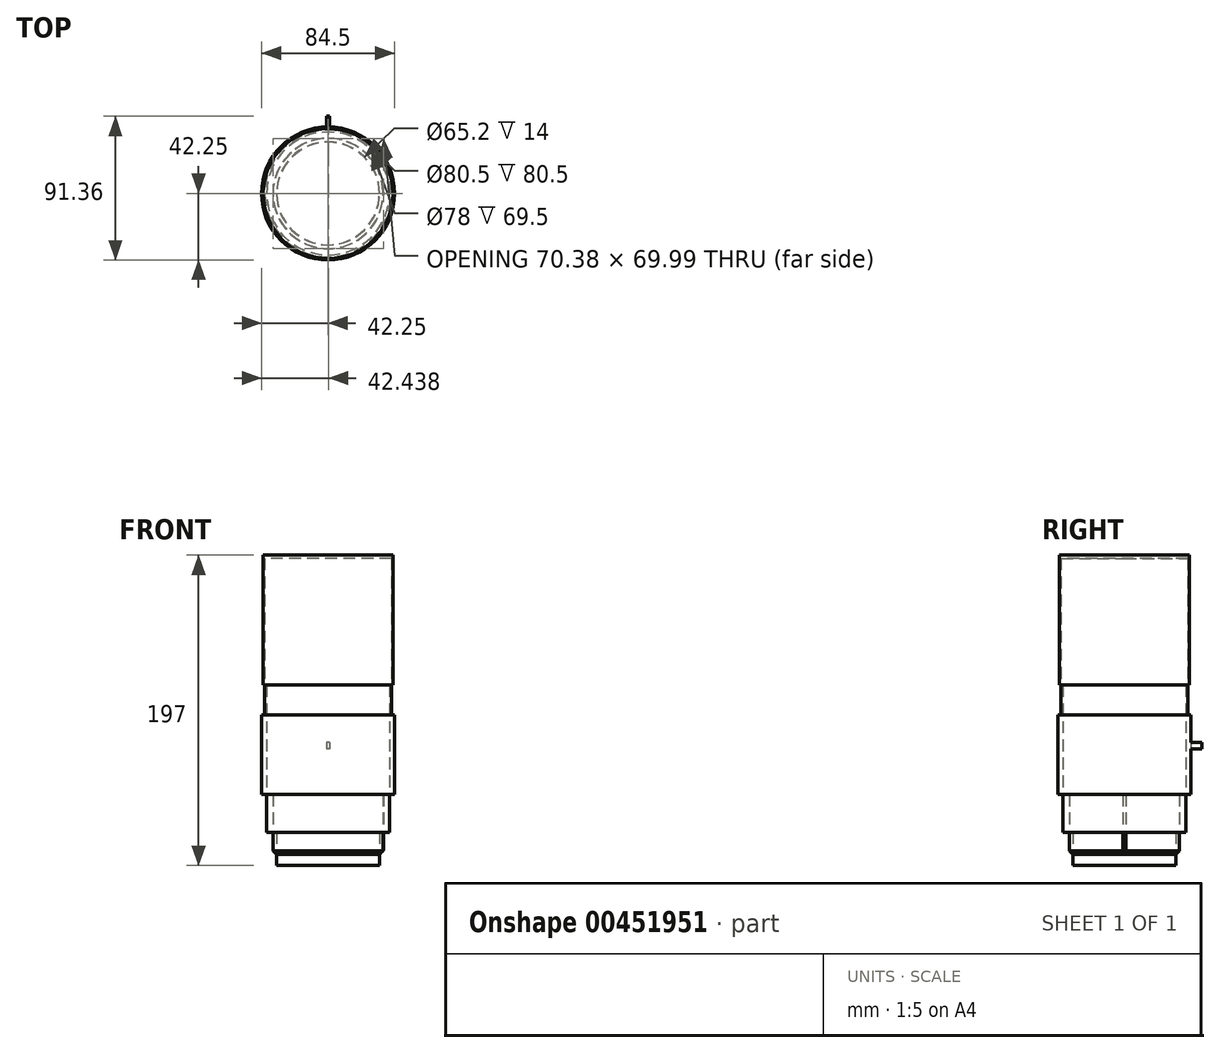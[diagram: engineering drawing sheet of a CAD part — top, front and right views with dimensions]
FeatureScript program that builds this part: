
annotation { "Feature Type Name" : "Feature", "Feature Type Description" : "" }
export const myFeature = defineFeature(function(context is Context, id is Id, definition is map)
    precondition{}
    {
        {
            var Q0;
            Q0=qCreatedBy(makeId("Top.planeOp"),FACE);
            var sketch = newSketch(context, id + "F0", { "sketchPlane" : qUnion([Q0])});
            skCircle(sketch, "E0", {"center": v(0, 0) * mm, "radius": 32.6 * mm});
            skSolve(sketch);
        }
        {
            var Q0;
            Q0=makeQuery(id+"F0.imprint","IMPRINT",FACE,{"disambiguationData":[TD([[makeQuery(id+"F0.imprint","IMPRINT",EDGE,{"derivedFrom":sQuery(id+"F0.wireOp",EDGE,"E0")}),1.0]])]});
            extrude(context, id + "F1", {"entities" : qUnion([Q0]), "depth" : 7 * mm});
        }
        {
            var Q0;
            Q0=makeQuery(id+"F1.opExtrude","CAP_FACE",FACE,{"disambiguationData":[OSD([sQuery(id+"F0.wireOp",EDGE,"E0")])],"isStart":false});
            var sketch = newSketch(context, id + "F2", { "sketchPlane" : qUnion([Q0])});
            skCircle(sketch, "E1", {"center": v(0, 0) * mm, "radius": 35 * mm});
            skSolve(sketch);
        }
        {
            var Q0;
            Q0=makeQuery(id+"F2.imprint","IMPRINT",FACE,{"disambiguationData":[TD([[makeQuery(id+"F2.imprint","IMPRINT",EDGE,{"derivedFrom":sQuery(id+"F2.wireOp",EDGE,"E1")}),1.0]])]});
            extrude(context, id + "F3", {"entities" : qUnion([Q0]), "depth" : 14 * mm});
        }
        {
            var Q0;
            Q0=makeQuery(id+"F3.opExtrude","CAP_EDGE",EDGE,{"disambiguationData":[OSD([sQuery(id+"F2.wireOp",EDGE,"E1")])],"isStart":true});
            chamfer(context, id + "F4", {"entities" : qUnion([Q0]), "chamferType" : ChamferType.OFFSET_ANGLE, "width" : 2.3 * mm, "oppositeDirection" : false, "angle" : 45 * degree, "tangentPropagation" : true});
        }
        {
            var Q0;
            Q0=makeQuery(id+"F3.opExtrude","CAP_FACE",FACE,{"disambiguationData":[OSD([sQuery(id+"F0.wireOp",EDGE,"E0"),sQuery(id+"F2.wireOp",EDGE,"E1")])],"isStart":false});
            var sketch = newSketch(context, id + "F5", { "sketchPlane" : qUnion([Q0])});
            skLineSegment(sketch, "E2.bottom", {"start": v(35.38, 0.9) * mm, "end": v(34.08, 0.9) * mm});
            skLineSegment(sketch, "E2.top", {"start": v(35.38, -0.9) * mm, "end": v(34.08, -0.9) * mm});
            skLineSegment(sketch, "E2.left", {"start": v(35.38, 0.9) * mm, "end": v(35.38, -0.9) * mm});
            skLineSegment(sketch, "E2.right", {"start": v(34.08, 0.9) * mm, "end": v(34.08, -0.9) * mm});
            skSolve(sketch);
        }
        {
            var Q0;
            Q0=qCreatedBy(makeId("Front.planeOp"),FACE);
            var sketch = newSketch(context, id + "F6", { "sketchPlane" : qUnion([Q0])});
            skLineSegment(sketch, "E3", {"start": v(0, 0) * mm, "end": v(0, 41.82) * mm});
            skSolve(sketch);
        }
        {
            var Q0;
            Q0=makeQuery(id+"FMMGtIccV8ZqxvP_2.16.F5.imprint","IMPRINT",FACE,{"disambiguationData":[TD([[makeQuery(id+"FMMGtIccV8ZqxvP_2.16.F5.imprint","IMPRINT",EDGE,{"derivedFrom":sQuery(id+"FMMGtIccV8ZqxvP_2.16.F5.wireOp",EDGE,"E2.bottom")}),1.0]])]});
            var Q1;
            Q1=makeQuery(id+"FMMGtIccV8ZqxvP_2.15.F5.imprint","IMPRINT",FACE,{"disambiguationData":[TD([[makeQuery(id+"FMMGtIccV8ZqxvP_2.15.F5.imprint","IMPRINT",EDGE,{"derivedFrom":sQuery(id+"FMMGtIccV8ZqxvP_2.15.F5.wireOp",EDGE,"E2.bottom")}),1.0]])]});
            var Q2;
            Q2=makeQuery(id+"FMMGtIccV8ZqxvP_2.14.F5.imprint","IMPRINT",FACE,{"disambiguationData":[TD([[makeQuery(id+"FMMGtIccV8ZqxvP_2.14.F5.imprint","IMPRINT",EDGE,{"derivedFrom":sQuery(id+"FMMGtIccV8ZqxvP_2.14.F5.wireOp",EDGE,"E2.bottom")}),1.0]])]});
            var Q3;
            Q3=makeQuery(id+"FMMGtIccV8ZqxvP_2.13.F5.imprint","IMPRINT",FACE,{"disambiguationData":[TD([[makeQuery(id+"FMMGtIccV8ZqxvP_2.13.F5.imprint","IMPRINT",EDGE,{"derivedFrom":sQuery(id+"FMMGtIccV8ZqxvP_2.13.F5.wireOp",EDGE,"E2.bottom")}),1.0]])]});
            var Q4;
            Q4=makeQuery(id+"FMMGtIccV8ZqxvP_2.12.F5.imprint","IMPRINT",FACE,{"disambiguationData":[TD([[makeQuery(id+"FMMGtIccV8ZqxvP_2.12.F5.imprint","IMPRINT",EDGE,{"derivedFrom":sQuery(id+"FMMGtIccV8ZqxvP_2.12.F5.wireOp",EDGE,"E2.bottom")}),1.0]])]});
            var Q5;
            Q5=makeQuery(id+"FMMGtIccV8ZqxvP_2.11.F5.imprint","IMPRINT",FACE,{"disambiguationData":[TD([[makeQuery(id+"FMMGtIccV8ZqxvP_2.11.F5.imprint","IMPRINT",EDGE,{"derivedFrom":sQuery(id+"FMMGtIccV8ZqxvP_2.11.F5.wireOp",EDGE,"E2.bottom")}),1.0]])]});
            var Q6;
            Q6=makeQuery(id+"FMMGtIccV8ZqxvP_2.10.F5.imprint","IMPRINT",FACE,{"disambiguationData":[TD([[makeQuery(id+"FMMGtIccV8ZqxvP_2.10.F5.imprint","IMPRINT",EDGE,{"derivedFrom":sQuery(id+"FMMGtIccV8ZqxvP_2.10.F5.wireOp",EDGE,"E2.bottom")}),1.0]])]});
            var Q7;
            Q7=makeQuery(id+"FMMGtIccV8ZqxvP_2.9.F5.imprint","IMPRINT",FACE,{"disambiguationData":[TD([[makeQuery(id+"FMMGtIccV8ZqxvP_2.9.F5.imprint","IMPRINT",EDGE,{"derivedFrom":sQuery(id+"FMMGtIccV8ZqxvP_2.9.F5.wireOp",EDGE,"E2.bottom")}),1.0]])]});
            var Q8;
            Q8=makeQuery(id+"FMMGtIccV8ZqxvP_2.8.F5.imprint","IMPRINT",FACE,{"disambiguationData":[TD([[makeQuery(id+"FMMGtIccV8ZqxvP_2.8.F5.imprint","IMPRINT",EDGE,{"derivedFrom":sQuery(id+"FMMGtIccV8ZqxvP_2.8.F5.wireOp",EDGE,"E2.bottom")}),1.0]])]});
            var Q9;
            Q9=makeQuery(id+"FMMGtIccV8ZqxvP_2.7.F5.imprint","IMPRINT",FACE,{"disambiguationData":[TD([[makeQuery(id+"FMMGtIccV8ZqxvP_2.7.F5.imprint","IMPRINT",EDGE,{"derivedFrom":sQuery(id+"FMMGtIccV8ZqxvP_2.7.F5.wireOp",EDGE,"E2.bottom")}),1.0]])]});
            var Q10;
            Q10=makeQuery(id+"FMMGtIccV8ZqxvP_2.6.F5.imprint","IMPRINT",FACE,{"disambiguationData":[TD([[makeQuery(id+"FMMGtIccV8ZqxvP_2.6.F5.imprint","IMPRINT",EDGE,{"derivedFrom":sQuery(id+"FMMGtIccV8ZqxvP_2.6.F5.wireOp",EDGE,"E2.bottom")}),1.0]])]});
            var Q11;
            Q11=makeQuery(id+"FMMGtIccV8ZqxvP_2.5.F5.imprint","IMPRINT",FACE,{"disambiguationData":[TD([[makeQuery(id+"FMMGtIccV8ZqxvP_2.5.F5.imprint","IMPRINT",EDGE,{"derivedFrom":sQuery(id+"FMMGtIccV8ZqxvP_2.5.F5.wireOp",EDGE,"E2.bottom")}),1.0]])]});
            var Q12;
            Q12=makeQuery(id+"FMMGtIccV8ZqxvP_2.4.F5.imprint","IMPRINT",FACE,{"disambiguationData":[TD([[makeQuery(id+"FMMGtIccV8ZqxvP_2.4.F5.imprint","IMPRINT",EDGE,{"derivedFrom":sQuery(id+"FMMGtIccV8ZqxvP_2.4.F5.wireOp",EDGE,"E2.bottom")}),1.0]])]});
            var Q13;
            Q13=makeQuery(id+"FMMGtIccV8ZqxvP_2.3.F5.imprint","IMPRINT",FACE,{"disambiguationData":[TD([[makeQuery(id+"FMMGtIccV8ZqxvP_2.3.F5.imprint","IMPRINT",EDGE,{"derivedFrom":sQuery(id+"FMMGtIccV8ZqxvP_2.3.F5.wireOp",EDGE,"E2.bottom")}),1.0]])]});
            var Q14;
            Q14=makeQuery(id+"FMMGtIccV8ZqxvP_2.2.F5.imprint","IMPRINT",FACE,{"disambiguationData":[TD([[makeQuery(id+"FMMGtIccV8ZqxvP_2.2.F5.imprint","IMPRINT",EDGE,{"derivedFrom":sQuery(id+"FMMGtIccV8ZqxvP_2.2.F5.wireOp",EDGE,"E2.bottom")}),1.0]])]});
            var Q15;
            Q15=makeQuery(id+"FMMGtIccV8ZqxvP_2.1.F5.imprint","IMPRINT",FACE,{"disambiguationData":[TD([[makeQuery(id+"FMMGtIccV8ZqxvP_2.1.F5.imprint","IMPRINT",EDGE,{"derivedFrom":sQuery(id+"FMMGtIccV8ZqxvP_2.1.F5.wireOp",EDGE,"E2.bottom")}),1.0]])]});
            var Q16;
            Q16=makeQuery(id+"FMMGtIccV8ZqxvP_2.49.F5.imprint","IMPRINT",FACE,{"disambiguationData":[TD([[makeQuery(id+"FMMGtIccV8ZqxvP_2.49.F5.imprint","IMPRINT",EDGE,{"derivedFrom":sQuery(id+"FMMGtIccV8ZqxvP_2.49.F5.wireOp",EDGE,"E2.bottom")}),1.0]])]});
            var Q17;
            Q17=makeQuery(id+"FMMGtIccV8ZqxvP_2.48.F5.imprint","IMPRINT",FACE,{"disambiguationData":[TD([[makeQuery(id+"FMMGtIccV8ZqxvP_2.48.F5.imprint","IMPRINT",EDGE,{"derivedFrom":sQuery(id+"FMMGtIccV8ZqxvP_2.48.F5.wireOp",EDGE,"E2.bottom")}),1.0]])]});
            var Q18;
            Q18=makeQuery(id+"FMMGtIccV8ZqxvP_2.47.F5.imprint","IMPRINT",FACE,{"disambiguationData":[TD([[makeQuery(id+"FMMGtIccV8ZqxvP_2.47.F5.imprint","IMPRINT",EDGE,{"derivedFrom":sQuery(id+"FMMGtIccV8ZqxvP_2.47.F5.wireOp",EDGE,"E2.bottom")}),1.0]])]});
            var Q19;
            Q19=makeQuery(id+"FMMGtIccV8ZqxvP_2.46.F5.imprint","IMPRINT",FACE,{"disambiguationData":[TD([[makeQuery(id+"FMMGtIccV8ZqxvP_2.46.F5.imprint","IMPRINT",EDGE,{"derivedFrom":sQuery(id+"FMMGtIccV8ZqxvP_2.46.F5.wireOp",EDGE,"E2.bottom")}),1.0]])]});
            var Q20;
            Q20=makeQuery(id+"FMMGtIccV8ZqxvP_2.45.F5.imprint","IMPRINT",FACE,{"disambiguationData":[TD([[makeQuery(id+"FMMGtIccV8ZqxvP_2.45.F5.imprint","IMPRINT",EDGE,{"derivedFrom":sQuery(id+"FMMGtIccV8ZqxvP_2.45.F5.wireOp",EDGE,"E2.bottom")}),1.0]])]});
            var Q21;
            Q21=makeQuery(id+"FMMGtIccV8ZqxvP_2.44.F5.imprint","IMPRINT",FACE,{"disambiguationData":[TD([[makeQuery(id+"FMMGtIccV8ZqxvP_2.44.F5.imprint","IMPRINT",EDGE,{"derivedFrom":sQuery(id+"FMMGtIccV8ZqxvP_2.44.F5.wireOp",EDGE,"E2.bottom")}),1.0]])]});
            var Q22;
            Q22=makeQuery(id+"FMMGtIccV8ZqxvP_2.43.F5.imprint","IMPRINT",FACE,{"disambiguationData":[TD([[makeQuery(id+"FMMGtIccV8ZqxvP_2.43.F5.imprint","IMPRINT",EDGE,{"derivedFrom":sQuery(id+"FMMGtIccV8ZqxvP_2.43.F5.wireOp",EDGE,"E2.bottom")}),1.0]])]});
            var Q23;
            Q23=makeQuery(id+"FMMGtIccV8ZqxvP_2.42.F5.imprint","IMPRINT",FACE,{"disambiguationData":[TD([[makeQuery(id+"FMMGtIccV8ZqxvP_2.42.F5.imprint","IMPRINT",EDGE,{"derivedFrom":sQuery(id+"FMMGtIccV8ZqxvP_2.42.F5.wireOp",EDGE,"E2.bottom")}),1.0]])]});
            var Q24;
            Q24=makeQuery(id+"FMMGtIccV8ZqxvP_2.40.F5.imprint","IMPRINT",FACE,{"disambiguationData":[TD([[makeQuery(id+"FMMGtIccV8ZqxvP_2.40.F5.imprint","IMPRINT",EDGE,{"derivedFrom":sQuery(id+"FMMGtIccV8ZqxvP_2.40.F5.wireOp",EDGE,"E2.bottom")}),1.0]])]});
            var Q25;
            Q25=makeQuery(id+"FMMGtIccV8ZqxvP_2.39.F5.imprint","IMPRINT",FACE,{"disambiguationData":[TD([[makeQuery(id+"FMMGtIccV8ZqxvP_2.39.F5.imprint","IMPRINT",EDGE,{"derivedFrom":sQuery(id+"FMMGtIccV8ZqxvP_2.39.F5.wireOp",EDGE,"E2.bottom")}),1.0]])]});
            var Q26;
            Q26=makeQuery(id+"FMMGtIccV8ZqxvP_2.38.F5.imprint","IMPRINT",FACE,{"disambiguationData":[TD([[makeQuery(id+"FMMGtIccV8ZqxvP_2.38.F5.imprint","IMPRINT",EDGE,{"derivedFrom":sQuery(id+"FMMGtIccV8ZqxvP_2.38.F5.wireOp",EDGE,"E2.bottom")}),1.0]])]});
            var Q27;
            Q27=makeQuery(id+"FMMGtIccV8ZqxvP_2.37.F5.imprint","IMPRINT",FACE,{"disambiguationData":[TD([[makeQuery(id+"FMMGtIccV8ZqxvP_2.37.F5.imprint","IMPRINT",EDGE,{"derivedFrom":sQuery(id+"FMMGtIccV8ZqxvP_2.37.F5.wireOp",EDGE,"E2.bottom")}),1.0]])]});
            var Q28;
            Q28=makeQuery(id+"FMMGtIccV8ZqxvP_2.36.F5.imprint","IMPRINT",FACE,{"disambiguationData":[TD([[makeQuery(id+"FMMGtIccV8ZqxvP_2.36.F5.imprint","IMPRINT",EDGE,{"derivedFrom":sQuery(id+"FMMGtIccV8ZqxvP_2.36.F5.wireOp",EDGE,"E2.bottom")}),1.0]])]});
            var Q29;
            Q29=makeQuery(id+"FMMGtIccV8ZqxvP_2.35.F5.imprint","IMPRINT",FACE,{"disambiguationData":[TD([[makeQuery(id+"FMMGtIccV8ZqxvP_2.35.F5.imprint","IMPRINT",EDGE,{"derivedFrom":sQuery(id+"FMMGtIccV8ZqxvP_2.35.F5.wireOp",EDGE,"E2.bottom")}),1.0]])]});
            var Q30;
            Q30=makeQuery(id+"FMMGtIccV8ZqxvP_2.34.F5.imprint","IMPRINT",FACE,{"disambiguationData":[TD([[makeQuery(id+"FMMGtIccV8ZqxvP_2.34.F5.imprint","IMPRINT",EDGE,{"derivedFrom":sQuery(id+"FMMGtIccV8ZqxvP_2.34.F5.wireOp",EDGE,"E2.bottom")}),1.0]])]});
            var Q31;
            Q31=makeQuery(id+"FMMGtIccV8ZqxvP_2.33.F5.imprint","IMPRINT",FACE,{"disambiguationData":[TD([[makeQuery(id+"FMMGtIccV8ZqxvP_2.33.F5.imprint","IMPRINT",EDGE,{"derivedFrom":sQuery(id+"FMMGtIccV8ZqxvP_2.33.F5.wireOp",EDGE,"E2.bottom")}),1.0]])]});
            var Q32;
            Q32=makeQuery(id+"FMMGtIccV8ZqxvP_2.32.F5.imprint","IMPRINT",FACE,{"disambiguationData":[TD([[makeQuery(id+"FMMGtIccV8ZqxvP_2.32.F5.imprint","IMPRINT",EDGE,{"derivedFrom":sQuery(id+"FMMGtIccV8ZqxvP_2.32.F5.wireOp",EDGE,"E2.bottom")}),1.0]])]});
            var Q33;
            Q33=makeQuery(id+"FMMGtIccV8ZqxvP_2.31.F5.imprint","IMPRINT",FACE,{"disambiguationData":[TD([[makeQuery(id+"FMMGtIccV8ZqxvP_2.31.F5.imprint","IMPRINT",EDGE,{"derivedFrom":sQuery(id+"FMMGtIccV8ZqxvP_2.31.F5.wireOp",EDGE,"E2.bottom")}),1.0]])]});
            var Q34;
            Q34=makeQuery(id+"FMMGtIccV8ZqxvP_2.30.F5.imprint","IMPRINT",FACE,{"disambiguationData":[TD([[makeQuery(id+"FMMGtIccV8ZqxvP_2.30.F5.imprint","IMPRINT",EDGE,{"derivedFrom":sQuery(id+"FMMGtIccV8ZqxvP_2.30.F5.wireOp",EDGE,"E2.bottom")}),1.0]])]});
            var Q35;
            Q35=makeQuery(id+"FMMGtIccV8ZqxvP_2.29.F5.imprint","IMPRINT",FACE,{"disambiguationData":[TD([[makeQuery(id+"FMMGtIccV8ZqxvP_2.29.F5.imprint","IMPRINT",EDGE,{"derivedFrom":sQuery(id+"FMMGtIccV8ZqxvP_2.29.F5.wireOp",EDGE,"E2.bottom")}),1.0]])]});
            var Q36;
            Q36=makeQuery(id+"FMMGtIccV8ZqxvP_2.28.F5.imprint","IMPRINT",FACE,{"disambiguationData":[TD([[makeQuery(id+"FMMGtIccV8ZqxvP_2.28.F5.imprint","IMPRINT",EDGE,{"derivedFrom":sQuery(id+"FMMGtIccV8ZqxvP_2.28.F5.wireOp",EDGE,"E2.bottom")}),1.0]])]});
            var Q37;
            Q37=makeQuery(id+"FMMGtIccV8ZqxvP_2.27.F5.imprint","IMPRINT",FACE,{"disambiguationData":[TD([[makeQuery(id+"FMMGtIccV8ZqxvP_2.27.F5.imprint","IMPRINT",EDGE,{"derivedFrom":sQuery(id+"FMMGtIccV8ZqxvP_2.27.F5.wireOp",EDGE,"E2.bottom")}),1.0]])]});
            var Q38;
            Q38=makeQuery(id+"FMMGtIccV8ZqxvP_2.26.F5.imprint","IMPRINT",FACE,{"disambiguationData":[TD([[makeQuery(id+"FMMGtIccV8ZqxvP_2.26.F5.imprint","IMPRINT",EDGE,{"derivedFrom":sQuery(id+"FMMGtIccV8ZqxvP_2.26.F5.wireOp",EDGE,"E2.bottom")}),1.0]])]});
            var Q39;
            Q39=makeQuery(id+"FMMGtIccV8ZqxvP_2.25.F5.imprint","IMPRINT",FACE,{"disambiguationData":[TD([[makeQuery(id+"FMMGtIccV8ZqxvP_2.25.F5.imprint","IMPRINT",EDGE,{"derivedFrom":sQuery(id+"FMMGtIccV8ZqxvP_2.25.F5.wireOp",EDGE,"E2.bottom")}),1.0]])]});
            var Q40;
            Q40=makeQuery(id+"FMMGtIccV8ZqxvP_2.24.F5.imprint","IMPRINT",FACE,{"disambiguationData":[TD([[makeQuery(id+"FMMGtIccV8ZqxvP_2.24.F5.imprint","IMPRINT",EDGE,{"derivedFrom":sQuery(id+"FMMGtIccV8ZqxvP_2.24.F5.wireOp",EDGE,"E2.bottom")}),1.0]])]});
            var Q41;
            Q41=makeQuery(id+"FMMGtIccV8ZqxvP_2.41.F5.imprint","IMPRINT",FACE,{"disambiguationData":[TD([[makeQuery(id+"FMMGtIccV8ZqxvP_2.41.F5.imprint","IMPRINT",EDGE,{"derivedFrom":sQuery(id+"FMMGtIccV8ZqxvP_2.41.F5.wireOp",EDGE,"E2.bottom")}),1.0]])]});
            var Q42;
            {var subQ0=sQuery(id+"F5.wireOp",EDGE,"E2.right");Q42=makeQuery(id+"F5.imprint","IMPRINT",FACE,{"disambiguationData":[TD([[makeQuery(id+"F5.imprint","IMPRINT",EDGE,{"derivedFrom":subQ0}),-1.0]])]});}
            var Q43;
            Q43=makeQuery(id+"FMMGtIccV8ZqxvP_2.23.F5.imprint","IMPRINT",FACE,{"disambiguationData":[TD([[makeQuery(id+"FMMGtIccV8ZqxvP_2.23.F5.imprint","IMPRINT",EDGE,{"derivedFrom":sQuery(id+"FMMGtIccV8ZqxvP_2.23.F5.wireOp",EDGE,"E2.bottom")}),1.0]])]});
            var Q44;
            Q44=makeQuery(id+"FMMGtIccV8ZqxvP_2.22.F5.imprint","IMPRINT",FACE,{"disambiguationData":[TD([[makeQuery(id+"FMMGtIccV8ZqxvP_2.22.F5.imprint","IMPRINT",EDGE,{"derivedFrom":sQuery(id+"FMMGtIccV8ZqxvP_2.22.F5.wireOp",EDGE,"E2.bottom")}),1.0]])]});
            var Q45;
            Q45=makeQuery(id+"FMMGtIccV8ZqxvP_2.21.F5.imprint","IMPRINT",FACE,{"disambiguationData":[TD([[makeQuery(id+"FMMGtIccV8ZqxvP_2.21.F5.imprint","IMPRINT",EDGE,{"derivedFrom":sQuery(id+"FMMGtIccV8ZqxvP_2.21.F5.wireOp",EDGE,"E2.bottom")}),1.0]])]});
            var Q46;
            Q46=makeQuery(id+"FMMGtIccV8ZqxvP_2.20.F5.imprint","IMPRINT",FACE,{"disambiguationData":[TD([[makeQuery(id+"FMMGtIccV8ZqxvP_2.20.F5.imprint","IMPRINT",EDGE,{"derivedFrom":sQuery(id+"FMMGtIccV8ZqxvP_2.20.F5.wireOp",EDGE,"E2.bottom")}),1.0]])]});
            var Q47;
            Q47=makeQuery(id+"FMMGtIccV8ZqxvP_2.19.F5.imprint","IMPRINT",FACE,{"disambiguationData":[TD([[makeQuery(id+"FMMGtIccV8ZqxvP_2.19.F5.imprint","IMPRINT",EDGE,{"derivedFrom":sQuery(id+"FMMGtIccV8ZqxvP_2.19.F5.wireOp",EDGE,"E2.bottom")}),1.0]])]});
            var Q48;
            Q48=makeQuery(id+"FMMGtIccV8ZqxvP_2.18.F5.imprint","IMPRINT",FACE,{"disambiguationData":[TD([[makeQuery(id+"FMMGtIccV8ZqxvP_2.18.F5.imprint","IMPRINT",EDGE,{"derivedFrom":sQuery(id+"FMMGtIccV8ZqxvP_2.18.F5.wireOp",EDGE,"E2.bottom")}),1.0]])]});
            var Q49;
            Q49=makeQuery(id+"FMMGtIccV8ZqxvP_2.17.F5.imprint","IMPRINT",FACE,{"disambiguationData":[TD([[makeQuery(id+"FMMGtIccV8ZqxvP_2.17.F5.imprint","IMPRINT",EDGE,{"derivedFrom":sQuery(id+"FMMGtIccV8ZqxvP_2.17.F5.wireOp",EDGE,"E2.bottom")}),1.0]])]});
            var Q50;
            {var subQ0=sQuery(id+"F5.wireOp",EDGE,"E2.right");Q50=makeQuery(id+"F5.imprint","IMPRINT",FACE,{"disambiguationData":[TD([[makeQuery(id+"F5.imprint","IMPRINT",EDGE,{"derivedFrom":subQ0}),1.0]])]});}
            var Q51;
            {var subQ0=sQuery(id+"F5.wireOp",EDGE,"E2.left");Q51=makeQuery(id+"F5.imprint","IMPRINT",FACE,{"disambiguationData":[TD([[makeQuery(id+"F5.imprint","IMPRINT",EDGE,{"derivedFrom":subQ0}),-1.0]])]});}
            extrude(context, id + "F7", {"entities" : qUnion([Q0, Q1, Q2, Q3, Q4, Q5, Q6, Q7, Q8, Q9, Q10, Q11, Q12, Q13, Q14, Q15, Q16, Q17, Q18, Q19, Q20, Q21, Q22, Q23, Q24, Q25, Q26, Q27, Q28, Q29, Q30, Q31, Q32, Q33, Q34, Q35, Q36, Q37, Q38, Q39, Q40, Q41, Q42, Q43, Q44, Q45, Q46, Q47, Q48, Q49, Q50, Q51]), "operationType" : NewBodyOperationType.ADD, "oppositeDirection" : true, "depth" : 11.5 * mm});
        }
        {
            var Q0;
            {var subQ0=sQuery(id+"F2.wireOp",EDGE,"E1");var subQ1=sQuery(id+"F0.wireOp",EDGE,"E0");Q0=makeQuery(id+"F7.boolean.opBoolean","MERGE",FACE,{"derivedFrom":[makeQuery(id+"F3.opExtrude","CAP_FACE",FACE,{"disambiguationData":[OSD([subQ1,subQ0])],"isStart":false}),makeQuery(id+"F7.opExtrude","CAP_FACE",FACE,{"disambiguationData":[OSD([subQ1,subQ0,sQuery(id+"F5.wireOp",EDGE,"E2.bottom"),sQuery(id+"F5.wireOp",EDGE,"E2.top"),sQuery(id+"F5.wireOp",EDGE,"E2.left")])],"isStart":true}),makeQuery(id+"F7.opExtrude","CAP_FACE",FACE,{"disambiguationData":[OSD([sQuery(id+"FMMGtIccV8ZqxvP_2.1.F5.wireOp",EDGE,"E2.bottom"),sQuery(id+"FMMGtIccV8ZqxvP_2.1.F5.wireOp",EDGE,"E2.top"),sQuery(id+"FMMGtIccV8ZqxvP_2.1.F5.wireOp",EDGE,"E2.left"),sQuery(id+"FMMGtIccV8ZqxvP_2.1.F5.wireOp",EDGE,"E2.right")])],"isStart":true}),makeQuery(id+"F7.opExtrude","CAP_FACE",FACE,{"disambiguationData":[OSD([sQuery(id+"FMMGtIccV8ZqxvP_2.2.F5.wireOp",EDGE,"E2.bottom"),sQuery(id+"FMMGtIccV8ZqxvP_2.2.F5.wireOp",EDGE,"E2.top"),sQuery(id+"FMMGtIccV8ZqxvP_2.2.F5.wireOp",EDGE,"E2.left"),sQuery(id+"FMMGtIccV8ZqxvP_2.2.F5.wireOp",EDGE,"E2.right")])],"isStart":true}),makeQuery(id+"F7.opExtrude","CAP_FACE",FACE,{"disambiguationData":[OSD([sQuery(id+"FMMGtIccV8ZqxvP_2.3.F5.wireOp",EDGE,"E2.bottom"),sQuery(id+"FMMGtIccV8ZqxvP_2.3.F5.wireOp",EDGE,"E2.top"),sQuery(id+"FMMGtIccV8ZqxvP_2.3.F5.wireOp",EDGE,"E2.left"),sQuery(id+"FMMGtIccV8ZqxvP_2.3.F5.wireOp",EDGE,"E2.right")])],"isStart":true}),makeQuery(id+"F7.opExtrude","CAP_FACE",FACE,{"disambiguationData":[OSD([sQuery(id+"FMMGtIccV8ZqxvP_2.4.F5.wireOp",EDGE,"E2.bottom"),sQuery(id+"FMMGtIccV8ZqxvP_2.4.F5.wireOp",EDGE,"E2.top"),sQuery(id+"FMMGtIccV8ZqxvP_2.4.F5.wireOp",EDGE,"E2.left"),sQuery(id+"FMMGtIccV8ZqxvP_2.4.F5.wireOp",EDGE,"E2.right")])],"isStart":true}),makeQuery(id+"F7.opExtrude","CAP_FACE",FACE,{"disambiguationData":[OSD([sQuery(id+"FMMGtIccV8ZqxvP_2.5.F5.wireOp",EDGE,"E2.bottom"),sQuery(id+"FMMGtIccV8ZqxvP_2.5.F5.wireOp",EDGE,"E2.top"),sQuery(id+"FMMGtIccV8ZqxvP_2.5.F5.wireOp",EDGE,"E2.left"),sQuery(id+"FMMGtIccV8ZqxvP_2.5.F5.wireOp",EDGE,"E2.right")])],"isStart":true}),makeQuery(id+"F7.opExtrude","CAP_FACE",FACE,{"disambiguationData":[OSD([sQuery(id+"FMMGtIccV8ZqxvP_2.6.F5.wireOp",EDGE,"E2.bottom"),sQuery(id+"FMMGtIccV8ZqxvP_2.6.F5.wireOp",EDGE,"E2.top"),sQuery(id+"FMMGtIccV8ZqxvP_2.6.F5.wireOp",EDGE,"E2.left"),sQuery(id+"FMMGtIccV8ZqxvP_2.6.F5.wireOp",EDGE,"E2.right")])],"isStart":true}),makeQuery(id+"F7.opExtrude","CAP_FACE",FACE,{"disambiguationData":[OSD([sQuery(id+"FMMGtIccV8ZqxvP_2.7.F5.wireOp",EDGE,"E2.bottom"),sQuery(id+"FMMGtIccV8ZqxvP_2.7.F5.wireOp",EDGE,"E2.top"),sQuery(id+"FMMGtIccV8ZqxvP_2.7.F5.wireOp",EDGE,"E2.left"),sQuery(id+"FMMGtIccV8ZqxvP_2.7.F5.wireOp",EDGE,"E2.right")])],"isStart":true}),makeQuery(id+"F7.opExtrude","CAP_FACE",FACE,{"disambiguationData":[OSD([sQuery(id+"FMMGtIccV8ZqxvP_2.8.F5.wireOp",EDGE,"E2.bottom"),sQuery(id+"FMMGtIccV8ZqxvP_2.8.F5.wireOp",EDGE,"E2.top"),sQuery(id+"FMMGtIccV8ZqxvP_2.8.F5.wireOp",EDGE,"E2.left"),sQuery(id+"FMMGtIccV8ZqxvP_2.8.F5.wireOp",EDGE,"E2.right")])],"isStart":true}),makeQuery(id+"F7.opExtrude","CAP_FACE",FACE,{"disambiguationData":[OSD([sQuery(id+"FMMGtIccV8ZqxvP_2.9.F5.wireOp",EDGE,"E2.bottom"),sQuery(id+"FMMGtIccV8ZqxvP_2.9.F5.wireOp",EDGE,"E2.top"),sQuery(id+"FMMGtIccV8ZqxvP_2.9.F5.wireOp",EDGE,"E2.left"),sQuery(id+"FMMGtIccV8ZqxvP_2.9.F5.wireOp",EDGE,"E2.right")])],"isStart":true}),makeQuery(id+"F7.opExtrude","CAP_FACE",FACE,{"disambiguationData":[OSD([sQuery(id+"FMMGtIccV8ZqxvP_2.10.F5.wireOp",EDGE,"E2.bottom"),sQuery(id+"FMMGtIccV8ZqxvP_2.10.F5.wireOp",EDGE,"E2.top"),sQuery(id+"FMMGtIccV8ZqxvP_2.10.F5.wireOp",EDGE,"E2.left"),sQuery(id+"FMMGtIccV8ZqxvP_2.10.F5.wireOp",EDGE,"E2.right")])],"isStart":true}),makeQuery(id+"F7.opExtrude","CAP_FACE",FACE,{"disambiguationData":[OSD([sQuery(id+"FMMGtIccV8ZqxvP_2.11.F5.wireOp",EDGE,"E2.bottom"),sQuery(id+"FMMGtIccV8ZqxvP_2.11.F5.wireOp",EDGE,"E2.top"),sQuery(id+"FMMGtIccV8ZqxvP_2.11.F5.wireOp",EDGE,"E2.left"),sQuery(id+"FMMGtIccV8ZqxvP_2.11.F5.wireOp",EDGE,"E2.right")])],"isStart":true}),makeQuery(id+"F7.opExtrude","CAP_FACE",FACE,{"disambiguationData":[OSD([sQuery(id+"FMMGtIccV8ZqxvP_2.12.F5.wireOp",EDGE,"E2.bottom"),sQuery(id+"FMMGtIccV8ZqxvP_2.12.F5.wireOp",EDGE,"E2.top"),sQuery(id+"FMMGtIccV8ZqxvP_2.12.F5.wireOp",EDGE,"E2.left"),sQuery(id+"FMMGtIccV8ZqxvP_2.12.F5.wireOp",EDGE,"E2.right")])],"isStart":true}),makeQuery(id+"F7.opExtrude","CAP_FACE",FACE,{"disambiguationData":[OSD([sQuery(id+"FMMGtIccV8ZqxvP_2.13.F5.wireOp",EDGE,"E2.bottom"),sQuery(id+"FMMGtIccV8ZqxvP_2.13.F5.wireOp",EDGE,"E2.top"),sQuery(id+"FMMGtIccV8ZqxvP_2.13.F5.wireOp",EDGE,"E2.left"),sQuery(id+"FMMGtIccV8ZqxvP_2.13.F5.wireOp",EDGE,"E2.right")])],"isStart":true}),makeQuery(id+"F7.opExtrude","CAP_FACE",FACE,{"disambiguationData":[OSD([sQuery(id+"FMMGtIccV8ZqxvP_2.14.F5.wireOp",EDGE,"E2.bottom"),sQuery(id+"FMMGtIccV8ZqxvP_2.14.F5.wireOp",EDGE,"E2.top"),sQuery(id+"FMMGtIccV8ZqxvP_2.14.F5.wireOp",EDGE,"E2.left"),sQuery(id+"FMMGtIccV8ZqxvP_2.14.F5.wireOp",EDGE,"E2.right")])],"isStart":true}),makeQuery(id+"F7.opExtrude","CAP_FACE",FACE,{"disambiguationData":[OSD([sQuery(id+"FMMGtIccV8ZqxvP_2.15.F5.wireOp",EDGE,"E2.bottom"),sQuery(id+"FMMGtIccV8ZqxvP_2.15.F5.wireOp",EDGE,"E2.top"),sQuery(id+"FMMGtIccV8ZqxvP_2.15.F5.wireOp",EDGE,"E2.left"),sQuery(id+"FMMGtIccV8ZqxvP_2.15.F5.wireOp",EDGE,"E2.right")])],"isStart":true}),makeQuery(id+"F7.opExtrude","CAP_FACE",FACE,{"disambiguationData":[OSD([sQuery(id+"FMMGtIccV8ZqxvP_2.16.F5.wireOp",EDGE,"E2.bottom"),sQuery(id+"FMMGtIccV8ZqxvP_2.16.F5.wireOp",EDGE,"E2.top"),sQuery(id+"FMMGtIccV8ZqxvP_2.16.F5.wireOp",EDGE,"E2.left"),sQuery(id+"FMMGtIccV8ZqxvP_2.16.F5.wireOp",EDGE,"E2.right")])],"isStart":true}),makeQuery(id+"F7.opExtrude","CAP_FACE",FACE,{"disambiguationData":[OSD([sQuery(id+"FMMGtIccV8ZqxvP_2.17.F5.wireOp",EDGE,"E2.bottom"),sQuery(id+"FMMGtIccV8ZqxvP_2.17.F5.wireOp",EDGE,"E2.top"),sQuery(id+"FMMGtIccV8ZqxvP_2.17.F5.wireOp",EDGE,"E2.left"),sQuery(id+"FMMGtIccV8ZqxvP_2.17.F5.wireOp",EDGE,"E2.right")])],"isStart":true}),makeQuery(id+"F7.opExtrude","CAP_FACE",FACE,{"disambiguationData":[OSD([sQuery(id+"FMMGtIccV8ZqxvP_2.18.F5.wireOp",EDGE,"E2.bottom"),sQuery(id+"FMMGtIccV8ZqxvP_2.18.F5.wireOp",EDGE,"E2.top"),sQuery(id+"FMMGtIccV8ZqxvP_2.18.F5.wireOp",EDGE,"E2.left"),sQuery(id+"FMMGtIccV8ZqxvP_2.18.F5.wireOp",EDGE,"E2.right")])],"isStart":true}),makeQuery(id+"F7.opExtrude","CAP_FACE",FACE,{"disambiguationData":[OSD([sQuery(id+"FMMGtIccV8ZqxvP_2.19.F5.wireOp",EDGE,"E2.bottom"),sQuery(id+"FMMGtIccV8ZqxvP_2.19.F5.wireOp",EDGE,"E2.top"),sQuery(id+"FMMGtIccV8ZqxvP_2.19.F5.wireOp",EDGE,"E2.left"),sQuery(id+"FMMGtIccV8ZqxvP_2.19.F5.wireOp",EDGE,"E2.right")])],"isStart":true}),makeQuery(id+"F7.opExtrude","CAP_FACE",FACE,{"disambiguationData":[OSD([sQuery(id+"FMMGtIccV8ZqxvP_2.20.F5.wireOp",EDGE,"E2.bottom"),sQuery(id+"FMMGtIccV8ZqxvP_2.20.F5.wireOp",EDGE,"E2.top"),sQuery(id+"FMMGtIccV8ZqxvP_2.20.F5.wireOp",EDGE,"E2.left"),sQuery(id+"FMMGtIccV8ZqxvP_2.20.F5.wireOp",EDGE,"E2.right")])],"isStart":true}),makeQuery(id+"F7.opExtrude","CAP_FACE",FACE,{"disambiguationData":[OSD([sQuery(id+"FMMGtIccV8ZqxvP_2.21.F5.wireOp",EDGE,"E2.bottom"),sQuery(id+"FMMGtIccV8ZqxvP_2.21.F5.wireOp",EDGE,"E2.top"),sQuery(id+"FMMGtIccV8ZqxvP_2.21.F5.wireOp",EDGE,"E2.left"),sQuery(id+"FMMGtIccV8ZqxvP_2.21.F5.wireOp",EDGE,"E2.right")])],"isStart":true}),makeQuery(id+"F7.opExtrude","CAP_FACE",FACE,{"disambiguationData":[OSD([sQuery(id+"FMMGtIccV8ZqxvP_2.22.F5.wireOp",EDGE,"E2.bottom"),sQuery(id+"FMMGtIccV8ZqxvP_2.22.F5.wireOp",EDGE,"E2.top"),sQuery(id+"FMMGtIccV8ZqxvP_2.22.F5.wireOp",EDGE,"E2.left"),sQuery(id+"FMMGtIccV8ZqxvP_2.22.F5.wireOp",EDGE,"E2.right")])],"isStart":true}),makeQuery(id+"F7.opExtrude","CAP_FACE",FACE,{"disambiguationData":[OSD([sQuery(id+"FMMGtIccV8ZqxvP_2.23.F5.wireOp",EDGE,"E2.bottom"),sQuery(id+"FMMGtIccV8ZqxvP_2.23.F5.wireOp",EDGE,"E2.top"),sQuery(id+"FMMGtIccV8ZqxvP_2.23.F5.wireOp",EDGE,"E2.left"),sQuery(id+"FMMGtIccV8ZqxvP_2.23.F5.wireOp",EDGE,"E2.right")])],"isStart":true}),makeQuery(id+"F7.opExtrude","CAP_FACE",FACE,{"disambiguationData":[OSD([sQuery(id+"FMMGtIccV8ZqxvP_2.24.F5.wireOp",EDGE,"E2.bottom"),sQuery(id+"FMMGtIccV8ZqxvP_2.24.F5.wireOp",EDGE,"E2.top"),sQuery(id+"FMMGtIccV8ZqxvP_2.24.F5.wireOp",EDGE,"E2.left"),sQuery(id+"FMMGtIccV8ZqxvP_2.24.F5.wireOp",EDGE,"E2.right")])],"isStart":true}),makeQuery(id+"F7.opExtrude","CAP_FACE",FACE,{"disambiguationData":[OSD([sQuery(id+"FMMGtIccV8ZqxvP_2.25.F5.wireOp",EDGE,"E2.bottom"),sQuery(id+"FMMGtIccV8ZqxvP_2.25.F5.wireOp",EDGE,"E2.top"),sQuery(id+"FMMGtIccV8ZqxvP_2.25.F5.wireOp",EDGE,"E2.left"),sQuery(id+"FMMGtIccV8ZqxvP_2.25.F5.wireOp",EDGE,"E2.right")])],"isStart":true}),makeQuery(id+"F7.opExtrude","CAP_FACE",FACE,{"disambiguationData":[OSD([sQuery(id+"FMMGtIccV8ZqxvP_2.26.F5.wireOp",EDGE,"E2.bottom"),sQuery(id+"FMMGtIccV8ZqxvP_2.26.F5.wireOp",EDGE,"E2.top"),sQuery(id+"FMMGtIccV8ZqxvP_2.26.F5.wireOp",EDGE,"E2.left"),sQuery(id+"FMMGtIccV8ZqxvP_2.26.F5.wireOp",EDGE,"E2.right")])],"isStart":true}),makeQuery(id+"F7.opExtrude","CAP_FACE",FACE,{"disambiguationData":[OSD([sQuery(id+"FMMGtIccV8ZqxvP_2.27.F5.wireOp",EDGE,"E2.bottom"),sQuery(id+"FMMGtIccV8ZqxvP_2.27.F5.wireOp",EDGE,"E2.top"),sQuery(id+"FMMGtIccV8ZqxvP_2.27.F5.wireOp",EDGE,"E2.left"),sQuery(id+"FMMGtIccV8ZqxvP_2.27.F5.wireOp",EDGE,"E2.right")])],"isStart":true}),makeQuery(id+"F7.opExtrude","CAP_FACE",FACE,{"disambiguationData":[OSD([sQuery(id+"FMMGtIccV8ZqxvP_2.28.F5.wireOp",EDGE,"E2.bottom"),sQuery(id+"FMMGtIccV8ZqxvP_2.28.F5.wireOp",EDGE,"E2.top"),sQuery(id+"FMMGtIccV8ZqxvP_2.28.F5.wireOp",EDGE,"E2.left"),sQuery(id+"FMMGtIccV8ZqxvP_2.28.F5.wireOp",EDGE,"E2.right")])],"isStart":true}),makeQuery(id+"F7.opExtrude","CAP_FACE",FACE,{"disambiguationData":[OSD([sQuery(id+"FMMGtIccV8ZqxvP_2.29.F5.wireOp",EDGE,"E2.bottom"),sQuery(id+"FMMGtIccV8ZqxvP_2.29.F5.wireOp",EDGE,"E2.top"),sQuery(id+"FMMGtIccV8ZqxvP_2.29.F5.wireOp",EDGE,"E2.left"),sQuery(id+"FMMGtIccV8ZqxvP_2.29.F5.wireOp",EDGE,"E2.right")])],"isStart":true}),makeQuery(id+"F7.opExtrude","CAP_FACE",FACE,{"disambiguationData":[OSD([sQuery(id+"FMMGtIccV8ZqxvP_2.30.F5.wireOp",EDGE,"E2.bottom"),sQuery(id+"FMMGtIccV8ZqxvP_2.30.F5.wireOp",EDGE,"E2.top"),sQuery(id+"FMMGtIccV8ZqxvP_2.30.F5.wireOp",EDGE,"E2.left"),sQuery(id+"FMMGtIccV8ZqxvP_2.30.F5.wireOp",EDGE,"E2.right")])],"isStart":true}),makeQuery(id+"F7.opExtrude","CAP_FACE",FACE,{"disambiguationData":[OSD([sQuery(id+"FMMGtIccV8ZqxvP_2.31.F5.wireOp",EDGE,"E2.bottom"),sQuery(id+"FMMGtIccV8ZqxvP_2.31.F5.wireOp",EDGE,"E2.top"),sQuery(id+"FMMGtIccV8ZqxvP_2.31.F5.wireOp",EDGE,"E2.left"),sQuery(id+"FMMGtIccV8ZqxvP_2.31.F5.wireOp",EDGE,"E2.right")])],"isStart":true}),makeQuery(id+"F7.opExtrude","CAP_FACE",FACE,{"disambiguationData":[OSD([sQuery(id+"FMMGtIccV8ZqxvP_2.32.F5.wireOp",EDGE,"E2.bottom"),sQuery(id+"FMMGtIccV8ZqxvP_2.32.F5.wireOp",EDGE,"E2.top"),sQuery(id+"FMMGtIccV8ZqxvP_2.32.F5.wireOp",EDGE,"E2.left"),sQuery(id+"FMMGtIccV8ZqxvP_2.32.F5.wireOp",EDGE,"E2.right")])],"isStart":true}),makeQuery(id+"F7.opExtrude","CAP_FACE",FACE,{"disambiguationData":[OSD([sQuery(id+"FMMGtIccV8ZqxvP_2.33.F5.wireOp",EDGE,"E2.bottom"),sQuery(id+"FMMGtIccV8ZqxvP_2.33.F5.wireOp",EDGE,"E2.top"),sQuery(id+"FMMGtIccV8ZqxvP_2.33.F5.wireOp",EDGE,"E2.left"),sQuery(id+"FMMGtIccV8ZqxvP_2.33.F5.wireOp",EDGE,"E2.right")])],"isStart":true}),makeQuery(id+"F7.opExtrude","CAP_FACE",FACE,{"disambiguationData":[OSD([sQuery(id+"FMMGtIccV8ZqxvP_2.34.F5.wireOp",EDGE,"E2.bottom"),sQuery(id+"FMMGtIccV8ZqxvP_2.34.F5.wireOp",EDGE,"E2.top"),sQuery(id+"FMMGtIccV8ZqxvP_2.34.F5.wireOp",EDGE,"E2.left"),sQuery(id+"FMMGtIccV8ZqxvP_2.34.F5.wireOp",EDGE,"E2.right")])],"isStart":true}),makeQuery(id+"F7.opExtrude","CAP_FACE",FACE,{"disambiguationData":[OSD([sQuery(id+"FMMGtIccV8ZqxvP_2.35.F5.wireOp",EDGE,"E2.bottom"),sQuery(id+"FMMGtIccV8ZqxvP_2.35.F5.wireOp",EDGE,"E2.top"),sQuery(id+"FMMGtIccV8ZqxvP_2.35.F5.wireOp",EDGE,"E2.left"),sQuery(id+"FMMGtIccV8ZqxvP_2.35.F5.wireOp",EDGE,"E2.right")])],"isStart":true}),makeQuery(id+"F7.opExtrude","CAP_FACE",FACE,{"disambiguationData":[OSD([sQuery(id+"FMMGtIccV8ZqxvP_2.36.F5.wireOp",EDGE,"E2.bottom"),sQuery(id+"FMMGtIccV8ZqxvP_2.36.F5.wireOp",EDGE,"E2.top"),sQuery(id+"FMMGtIccV8ZqxvP_2.36.F5.wireOp",EDGE,"E2.left"),sQuery(id+"FMMGtIccV8ZqxvP_2.36.F5.wireOp",EDGE,"E2.right")])],"isStart":true}),makeQuery(id+"F7.opExtrude","CAP_FACE",FACE,{"disambiguationData":[OSD([sQuery(id+"FMMGtIccV8ZqxvP_2.37.F5.wireOp",EDGE,"E2.bottom"),sQuery(id+"FMMGtIccV8ZqxvP_2.37.F5.wireOp",EDGE,"E2.top"),sQuery(id+"FMMGtIccV8ZqxvP_2.37.F5.wireOp",EDGE,"E2.left"),sQuery(id+"FMMGtIccV8ZqxvP_2.37.F5.wireOp",EDGE,"E2.right")])],"isStart":true}),makeQuery(id+"F7.opExtrude","CAP_FACE",FACE,{"disambiguationData":[OSD([sQuery(id+"FMMGtIccV8ZqxvP_2.38.F5.wireOp",EDGE,"E2.bottom"),sQuery(id+"FMMGtIccV8ZqxvP_2.38.F5.wireOp",EDGE,"E2.top"),sQuery(id+"FMMGtIccV8ZqxvP_2.38.F5.wireOp",EDGE,"E2.left"),sQuery(id+"FMMGtIccV8ZqxvP_2.38.F5.wireOp",EDGE,"E2.right")])],"isStart":true}),makeQuery(id+"F7.opExtrude","CAP_FACE",FACE,{"disambiguationData":[OSD([sQuery(id+"FMMGtIccV8ZqxvP_2.39.F5.wireOp",EDGE,"E2.bottom"),sQuery(id+"FMMGtIccV8ZqxvP_2.39.F5.wireOp",EDGE,"E2.top"),sQuery(id+"FMMGtIccV8ZqxvP_2.39.F5.wireOp",EDGE,"E2.left"),sQuery(id+"FMMGtIccV8ZqxvP_2.39.F5.wireOp",EDGE,"E2.right")])],"isStart":true}),makeQuery(id+"F7.opExtrude","CAP_FACE",FACE,{"disambiguationData":[OSD([sQuery(id+"FMMGtIccV8ZqxvP_2.40.F5.wireOp",EDGE,"E2.bottom"),sQuery(id+"FMMGtIccV8ZqxvP_2.40.F5.wireOp",EDGE,"E2.top"),sQuery(id+"FMMGtIccV8ZqxvP_2.40.F5.wireOp",EDGE,"E2.left"),sQuery(id+"FMMGtIccV8ZqxvP_2.40.F5.wireOp",EDGE,"E2.right")])],"isStart":true}),makeQuery(id+"F7.opExtrude","CAP_FACE",FACE,{"disambiguationData":[OSD([sQuery(id+"FMMGtIccV8ZqxvP_2.41.F5.wireOp",EDGE,"E2.bottom"),sQuery(id+"FMMGtIccV8ZqxvP_2.41.F5.wireOp",EDGE,"E2.top"),sQuery(id+"FMMGtIccV8ZqxvP_2.41.F5.wireOp",EDGE,"E2.left"),sQuery(id+"FMMGtIccV8ZqxvP_2.41.F5.wireOp",EDGE,"E2.right")])],"isStart":true}),makeQuery(id+"F7.opExtrude","CAP_FACE",FACE,{"disambiguationData":[OSD([sQuery(id+"FMMGtIccV8ZqxvP_2.42.F5.wireOp",EDGE,"E2.bottom"),sQuery(id+"FMMGtIccV8ZqxvP_2.42.F5.wireOp",EDGE,"E2.top"),sQuery(id+"FMMGtIccV8ZqxvP_2.42.F5.wireOp",EDGE,"E2.left"),sQuery(id+"FMMGtIccV8ZqxvP_2.42.F5.wireOp",EDGE,"E2.right")])],"isStart":true}),makeQuery(id+"F7.opExtrude","CAP_FACE",FACE,{"disambiguationData":[OSD([sQuery(id+"FMMGtIccV8ZqxvP_2.43.F5.wireOp",EDGE,"E2.bottom"),sQuery(id+"FMMGtIccV8ZqxvP_2.43.F5.wireOp",EDGE,"E2.top"),sQuery(id+"FMMGtIccV8ZqxvP_2.43.F5.wireOp",EDGE,"E2.left"),sQuery(id+"FMMGtIccV8ZqxvP_2.43.F5.wireOp",EDGE,"E2.right")])],"isStart":true}),makeQuery(id+"F7.opExtrude","CAP_FACE",FACE,{"disambiguationData":[OSD([sQuery(id+"FMMGtIccV8ZqxvP_2.44.F5.wireOp",EDGE,"E2.bottom"),sQuery(id+"FMMGtIccV8ZqxvP_2.44.F5.wireOp",EDGE,"E2.top"),sQuery(id+"FMMGtIccV8ZqxvP_2.44.F5.wireOp",EDGE,"E2.left"),sQuery(id+"FMMGtIccV8ZqxvP_2.44.F5.wireOp",EDGE,"E2.right")])],"isStart":true}),makeQuery(id+"F7.opExtrude","CAP_FACE",FACE,{"disambiguationData":[OSD([sQuery(id+"FMMGtIccV8ZqxvP_2.45.F5.wireOp",EDGE,"E2.bottom"),sQuery(id+"FMMGtIccV8ZqxvP_2.45.F5.wireOp",EDGE,"E2.top"),sQuery(id+"FMMGtIccV8ZqxvP_2.45.F5.wireOp",EDGE,"E2.left"),sQuery(id+"FMMGtIccV8ZqxvP_2.45.F5.wireOp",EDGE,"E2.right")])],"isStart":true}),makeQuery(id+"F7.opExtrude","CAP_FACE",FACE,{"disambiguationData":[OSD([sQuery(id+"FMMGtIccV8ZqxvP_2.46.F5.wireOp",EDGE,"E2.bottom"),sQuery(id+"FMMGtIccV8ZqxvP_2.46.F5.wireOp",EDGE,"E2.top"),sQuery(id+"FMMGtIccV8ZqxvP_2.46.F5.wireOp",EDGE,"E2.left"),sQuery(id+"FMMGtIccV8ZqxvP_2.46.F5.wireOp",EDGE,"E2.right")])],"isStart":true}),makeQuery(id+"F7.opExtrude","CAP_FACE",FACE,{"disambiguationData":[OSD([sQuery(id+"FMMGtIccV8ZqxvP_2.47.F5.wireOp",EDGE,"E2.bottom"),sQuery(id+"FMMGtIccV8ZqxvP_2.47.F5.wireOp",EDGE,"E2.top"),sQuery(id+"FMMGtIccV8ZqxvP_2.47.F5.wireOp",EDGE,"E2.left"),sQuery(id+"FMMGtIccV8ZqxvP_2.47.F5.wireOp",EDGE,"E2.right")])],"isStart":true}),makeQuery(id+"F7.opExtrude","CAP_FACE",FACE,{"disambiguationData":[OSD([sQuery(id+"FMMGtIccV8ZqxvP_2.48.F5.wireOp",EDGE,"E2.bottom"),sQuery(id+"FMMGtIccV8ZqxvP_2.48.F5.wireOp",EDGE,"E2.top"),sQuery(id+"FMMGtIccV8ZqxvP_2.48.F5.wireOp",EDGE,"E2.left"),sQuery(id+"FMMGtIccV8ZqxvP_2.48.F5.wireOp",EDGE,"E2.right")])],"isStart":true}),makeQuery(id+"F7.opExtrude","CAP_FACE",FACE,{"disambiguationData":[OSD([sQuery(id+"FMMGtIccV8ZqxvP_2.49.F5.wireOp",EDGE,"E2.bottom"),sQuery(id+"FMMGtIccV8ZqxvP_2.49.F5.wireOp",EDGE,"E2.top"),sQuery(id+"FMMGtIccV8ZqxvP_2.49.F5.wireOp",EDGE,"E2.left"),sQuery(id+"FMMGtIccV8ZqxvP_2.49.F5.wireOp",EDGE,"E2.right")])],"isStart":true})]});}
            var sketch = newSketch(context, id + "F8", { "sketchPlane" : qUnion([Q0])});
            skCircle(sketch, "E4", {"center": v(0, 0) * mm, "radius": 39 * mm});
            skSolve(sketch);
        }
        {
            var Q0;
            Q0=makeQuery(id+"F8.imprint","IMPRINT",FACE,{"disambiguationData":[TD([[makeQuery(id+"F8.imprint","IMPRINT",EDGE,{"derivedFrom":sQuery(id+"F8.wireOp",EDGE,"E4")}),1.0]])]});
            extrude(context, id + "F9", {"entities" : qUnion([Q0]), "depth" : 24 * mm});
        }
        {
            var Q0;
            Q0=makeQuery(id+"F9.opExtrude","CAP_FACE",FACE,{"disambiguationData":[OSD([sQuery(id+"F2.wireOp",EDGE,"E1"),sQuery(id+"F5.wireOp",EDGE,"E2.bottom"),sQuery(id+"F5.wireOp",EDGE,"E2.top"),sQuery(id+"F5.wireOp",EDGE,"E2.left"),sQuery(id+"FMMGtIccV8ZqxvP_2.1.F5.wireOp",EDGE,"E2.bottom"),sQuery(id+"FMMGtIccV8ZqxvP_2.1.F5.wireOp",EDGE,"E2.top"),sQuery(id+"FMMGtIccV8ZqxvP_2.1.F5.wireOp",EDGE,"E2.left"),sQuery(id+"FMMGtIccV8ZqxvP_2.2.F5.wireOp",EDGE,"E2.bottom"),sQuery(id+"FMMGtIccV8ZqxvP_2.2.F5.wireOp",EDGE,"E2.top"),sQuery(id+"FMMGtIccV8ZqxvP_2.2.F5.wireOp",EDGE,"E2.left"),sQuery(id+"FMMGtIccV8ZqxvP_2.3.F5.wireOp",EDGE,"E2.bottom"),sQuery(id+"FMMGtIccV8ZqxvP_2.3.F5.wireOp",EDGE,"E2.top"),sQuery(id+"FMMGtIccV8ZqxvP_2.3.F5.wireOp",EDGE,"E2.left"),sQuery(id+"FMMGtIccV8ZqxvP_2.4.F5.wireOp",EDGE,"E2.bottom"),sQuery(id+"FMMGtIccV8ZqxvP_2.4.F5.wireOp",EDGE,"E2.top"),sQuery(id+"FMMGtIccV8ZqxvP_2.4.F5.wireOp",EDGE,"E2.left"),sQuery(id+"FMMGtIccV8ZqxvP_2.5.F5.wireOp",EDGE,"E2.bottom"),sQuery(id+"FMMGtIccV8ZqxvP_2.5.F5.wireOp",EDGE,"E2.top"),sQuery(id+"FMMGtIccV8ZqxvP_2.5.F5.wireOp",EDGE,"E2.left"),sQuery(id+"FMMGtIccV8ZqxvP_2.6.F5.wireOp",EDGE,"E2.bottom"),sQuery(id+"FMMGtIccV8ZqxvP_2.6.F5.wireOp",EDGE,"E2.top"),sQuery(id+"FMMGtIccV8ZqxvP_2.6.F5.wireOp",EDGE,"E2.left"),sQuery(id+"FMMGtIccV8ZqxvP_2.7.F5.wireOp",EDGE,"E2.bottom"),sQuery(id+"FMMGtIccV8ZqxvP_2.7.F5.wireOp",EDGE,"E2.top"),sQuery(id+"FMMGtIccV8ZqxvP_2.7.F5.wireOp",EDGE,"E2.left"),sQuery(id+"FMMGtIccV8ZqxvP_2.8.F5.wireOp",EDGE,"E2.bottom"),sQuery(id+"FMMGtIccV8ZqxvP_2.8.F5.wireOp",EDGE,"E2.top"),sQuery(id+"FMMGtIccV8ZqxvP_2.8.F5.wireOp",EDGE,"E2.left"),sQuery(id+"FMMGtIccV8ZqxvP_2.9.F5.wireOp",EDGE,"E2.bottom"),sQuery(id+"FMMGtIccV8ZqxvP_2.9.F5.wireOp",EDGE,"E2.top"),sQuery(id+"FMMGtIccV8ZqxvP_2.9.F5.wireOp",EDGE,"E2.left"),sQuery(id+"FMMGtIccV8ZqxvP_2.10.F5.wireOp",EDGE,"E2.bottom"),sQuery(id+"FMMGtIccV8ZqxvP_2.10.F5.wireOp",EDGE,"E2.top"),sQuery(id+"FMMGtIccV8ZqxvP_2.10.F5.wireOp",EDGE,"E2.left"),sQuery(id+"FMMGtIccV8ZqxvP_2.11.F5.wireOp",EDGE,"E2.bottom"),sQuery(id+"FMMGtIccV8ZqxvP_2.11.F5.wireOp",EDGE,"E2.top"),sQuery(id+"FMMGtIccV8ZqxvP_2.11.F5.wireOp",EDGE,"E2.left"),sQuery(id+"FMMGtIccV8ZqxvP_2.12.F5.wireOp",EDGE,"E2.bottom"),sQuery(id+"FMMGtIccV8ZqxvP_2.12.F5.wireOp",EDGE,"E2.top"),sQuery(id+"FMMGtIccV8ZqxvP_2.12.F5.wireOp",EDGE,"E2.left"),sQuery(id+"FMMGtIccV8ZqxvP_2.13.F5.wireOp",EDGE,"E2.bottom"),sQuery(id+"FMMGtIccV8ZqxvP_2.13.F5.wireOp",EDGE,"E2.top"),sQuery(id+"FMMGtIccV8ZqxvP_2.13.F5.wireOp",EDGE,"E2.left"),sQuery(id+"FMMGtIccV8ZqxvP_2.14.F5.wireOp",EDGE,"E2.bottom"),sQuery(id+"FMMGtIccV8ZqxvP_2.14.F5.wireOp",EDGE,"E2.top"),sQuery(id+"FMMGtIccV8ZqxvP_2.14.F5.wireOp",EDGE,"E2.left"),sQuery(id+"FMMGtIccV8ZqxvP_2.15.F5.wireOp",EDGE,"E2.bottom"),sQuery(id+"FMMGtIccV8ZqxvP_2.15.F5.wireOp",EDGE,"E2.top"),sQuery(id+"FMMGtIccV8ZqxvP_2.15.F5.wireOp",EDGE,"E2.left"),sQuery(id+"FMMGtIccV8ZqxvP_2.16.F5.wireOp",EDGE,"E2.bottom"),sQuery(id+"FMMGtIccV8ZqxvP_2.16.F5.wireOp",EDGE,"E2.top"),sQuery(id+"FMMGtIccV8ZqxvP_2.16.F5.wireOp",EDGE,"E2.left"),sQuery(id+"FMMGtIccV8ZqxvP_2.17.F5.wireOp",EDGE,"E2.bottom"),sQuery(id+"FMMGtIccV8ZqxvP_2.17.F5.wireOp",EDGE,"E2.top"),sQuery(id+"FMMGtIccV8ZqxvP_2.17.F5.wireOp",EDGE,"E2.left"),sQuery(id+"FMMGtIccV8ZqxvP_2.18.F5.wireOp",EDGE,"E2.bottom"),sQuery(id+"FMMGtIccV8ZqxvP_2.18.F5.wireOp",EDGE,"E2.top"),sQuery(id+"FMMGtIccV8ZqxvP_2.18.F5.wireOp",EDGE,"E2.left"),sQuery(id+"FMMGtIccV8ZqxvP_2.19.F5.wireOp",EDGE,"E2.bottom"),sQuery(id+"FMMGtIccV8ZqxvP_2.19.F5.wireOp",EDGE,"E2.top"),sQuery(id+"FMMGtIccV8ZqxvP_2.19.F5.wireOp",EDGE,"E2.left"),sQuery(id+"FMMGtIccV8ZqxvP_2.20.F5.wireOp",EDGE,"E2.bottom"),sQuery(id+"FMMGtIccV8ZqxvP_2.20.F5.wireOp",EDGE,"E2.top"),sQuery(id+"FMMGtIccV8ZqxvP_2.20.F5.wireOp",EDGE,"E2.left"),sQuery(id+"FMMGtIccV8ZqxvP_2.21.F5.wireOp",EDGE,"E2.bottom"),sQuery(id+"FMMGtIccV8ZqxvP_2.21.F5.wireOp",EDGE,"E2.top"),sQuery(id+"FMMGtIccV8ZqxvP_2.21.F5.wireOp",EDGE,"E2.left"),sQuery(id+"FMMGtIccV8ZqxvP_2.22.F5.wireOp",EDGE,"E2.bottom"),sQuery(id+"FMMGtIccV8ZqxvP_2.22.F5.wireOp",EDGE,"E2.top"),sQuery(id+"FMMGtIccV8ZqxvP_2.22.F5.wireOp",EDGE,"E2.left"),sQuery(id+"FMMGtIccV8ZqxvP_2.23.F5.wireOp",EDGE,"E2.bottom"),sQuery(id+"FMMGtIccV8ZqxvP_2.23.F5.wireOp",EDGE,"E2.top"),sQuery(id+"FMMGtIccV8ZqxvP_2.23.F5.wireOp",EDGE,"E2.left"),sQuery(id+"FMMGtIccV8ZqxvP_2.24.F5.wireOp",EDGE,"E2.bottom"),sQuery(id+"FMMGtIccV8ZqxvP_2.24.F5.wireOp",EDGE,"E2.top"),sQuery(id+"FMMGtIccV8ZqxvP_2.24.F5.wireOp",EDGE,"E2.left"),sQuery(id+"FMMGtIccV8ZqxvP_2.25.F5.wireOp",EDGE,"E2.bottom"),sQuery(id+"FMMGtIccV8ZqxvP_2.25.F5.wireOp",EDGE,"E2.top"),sQuery(id+"FMMGtIccV8ZqxvP_2.25.F5.wireOp",EDGE,"E2.left"),sQuery(id+"FMMGtIccV8ZqxvP_2.26.F5.wireOp",EDGE,"E2.bottom"),sQuery(id+"FMMGtIccV8ZqxvP_2.26.F5.wireOp",EDGE,"E2.top"),sQuery(id+"FMMGtIccV8ZqxvP_2.26.F5.wireOp",EDGE,"E2.left"),sQuery(id+"FMMGtIccV8ZqxvP_2.27.F5.wireOp",EDGE,"E2.bottom"),sQuery(id+"FMMGtIccV8ZqxvP_2.27.F5.wireOp",EDGE,"E2.top"),sQuery(id+"FMMGtIccV8ZqxvP_2.27.F5.wireOp",EDGE,"E2.left"),sQuery(id+"FMMGtIccV8ZqxvP_2.28.F5.wireOp",EDGE,"E2.bottom"),sQuery(id+"FMMGtIccV8ZqxvP_2.28.F5.wireOp",EDGE,"E2.top"),sQuery(id+"FMMGtIccV8ZqxvP_2.28.F5.wireOp",EDGE,"E2.left"),sQuery(id+"FMMGtIccV8ZqxvP_2.29.F5.wireOp",EDGE,"E2.bottom"),sQuery(id+"FMMGtIccV8ZqxvP_2.29.F5.wireOp",EDGE,"E2.top"),sQuery(id+"FMMGtIccV8ZqxvP_2.29.F5.wireOp",EDGE,"E2.left"),sQuery(id+"FMMGtIccV8ZqxvP_2.30.F5.wireOp",EDGE,"E2.bottom"),sQuery(id+"FMMGtIccV8ZqxvP_2.30.F5.wireOp",EDGE,"E2.top"),sQuery(id+"FMMGtIccV8ZqxvP_2.30.F5.wireOp",EDGE,"E2.left"),sQuery(id+"FMMGtIccV8ZqxvP_2.31.F5.wireOp",EDGE,"E2.bottom"),sQuery(id+"FMMGtIccV8ZqxvP_2.31.F5.wireOp",EDGE,"E2.top"),sQuery(id+"FMMGtIccV8ZqxvP_2.31.F5.wireOp",EDGE,"E2.left"),sQuery(id+"FMMGtIccV8ZqxvP_2.32.F5.wireOp",EDGE,"E2.bottom"),sQuery(id+"FMMGtIccV8ZqxvP_2.32.F5.wireOp",EDGE,"E2.top"),sQuery(id+"FMMGtIccV8ZqxvP_2.32.F5.wireOp",EDGE,"E2.left"),sQuery(id+"FMMGtIccV8ZqxvP_2.33.F5.wireOp",EDGE,"E2.bottom"),sQuery(id+"FMMGtIccV8ZqxvP_2.33.F5.wireOp",EDGE,"E2.top"),sQuery(id+"FMMGtIccV8ZqxvP_2.33.F5.wireOp",EDGE,"E2.left"),sQuery(id+"FMMGtIccV8ZqxvP_2.34.F5.wireOp",EDGE,"E2.bottom"),sQuery(id+"FMMGtIccV8ZqxvP_2.34.F5.wireOp",EDGE,"E2.top"),sQuery(id+"FMMGtIccV8ZqxvP_2.34.F5.wireOp",EDGE,"E2.left"),sQuery(id+"FMMGtIccV8ZqxvP_2.35.F5.wireOp",EDGE,"E2.bottom"),sQuery(id+"FMMGtIccV8ZqxvP_2.35.F5.wireOp",EDGE,"E2.top"),sQuery(id+"FMMGtIccV8ZqxvP_2.35.F5.wireOp",EDGE,"E2.left"),sQuery(id+"FMMGtIccV8ZqxvP_2.36.F5.wireOp",EDGE,"E2.bottom"),sQuery(id+"FMMGtIccV8ZqxvP_2.36.F5.wireOp",EDGE,"E2.top"),sQuery(id+"FMMGtIccV8ZqxvP_2.36.F5.wireOp",EDGE,"E2.left"),sQuery(id+"FMMGtIccV8ZqxvP_2.37.F5.wireOp",EDGE,"E2.bottom"),sQuery(id+"FMMGtIccV8ZqxvP_2.37.F5.wireOp",EDGE,"E2.top"),sQuery(id+"FMMGtIccV8ZqxvP_2.37.F5.wireOp",EDGE,"E2.left"),sQuery(id+"FMMGtIccV8ZqxvP_2.38.F5.wireOp",EDGE,"E2.bottom"),sQuery(id+"FMMGtIccV8ZqxvP_2.38.F5.wireOp",EDGE,"E2.top"),sQuery(id+"FMMGtIccV8ZqxvP_2.38.F5.wireOp",EDGE,"E2.left"),sQuery(id+"FMMGtIccV8ZqxvP_2.39.F5.wireOp",EDGE,"E2.bottom"),sQuery(id+"FMMGtIccV8ZqxvP_2.39.F5.wireOp",EDGE,"E2.top"),sQuery(id+"FMMGtIccV8ZqxvP_2.39.F5.wireOp",EDGE,"E2.left"),sQuery(id+"FMMGtIccV8ZqxvP_2.40.F5.wireOp",EDGE,"E2.bottom"),sQuery(id+"FMMGtIccV8ZqxvP_2.40.F5.wireOp",EDGE,"E2.top"),sQuery(id+"FMMGtIccV8ZqxvP_2.40.F5.wireOp",EDGE,"E2.left"),sQuery(id+"FMMGtIccV8ZqxvP_2.41.F5.wireOp",EDGE,"E2.bottom"),sQuery(id+"FMMGtIccV8ZqxvP_2.41.F5.wireOp",EDGE,"E2.top"),sQuery(id+"FMMGtIccV8ZqxvP_2.41.F5.wireOp",EDGE,"E2.left"),sQuery(id+"FMMGtIccV8ZqxvP_2.42.F5.wireOp",EDGE,"E2.bottom"),sQuery(id+"FMMGtIccV8ZqxvP_2.42.F5.wireOp",EDGE,"E2.top"),sQuery(id+"FMMGtIccV8ZqxvP_2.42.F5.wireOp",EDGE,"E2.left"),sQuery(id+"FMMGtIccV8ZqxvP_2.43.F5.wireOp",EDGE,"E2.bottom"),sQuery(id+"FMMGtIccV8ZqxvP_2.43.F5.wireOp",EDGE,"E2.top"),sQuery(id+"FMMGtIccV8ZqxvP_2.43.F5.wireOp",EDGE,"E2.left"),sQuery(id+"FMMGtIccV8ZqxvP_2.44.F5.wireOp",EDGE,"E2.bottom"),sQuery(id+"FMMGtIccV8ZqxvP_2.44.F5.wireOp",EDGE,"E2.top"),sQuery(id+"FMMGtIccV8ZqxvP_2.44.F5.wireOp",EDGE,"E2.left"),sQuery(id+"FMMGtIccV8ZqxvP_2.45.F5.wireOp",EDGE,"E2.bottom"),sQuery(id+"FMMGtIccV8ZqxvP_2.45.F5.wireOp",EDGE,"E2.top"),sQuery(id+"FMMGtIccV8ZqxvP_2.45.F5.wireOp",EDGE,"E2.left"),sQuery(id+"FMMGtIccV8ZqxvP_2.46.F5.wireOp",EDGE,"E2.bottom"),sQuery(id+"FMMGtIccV8ZqxvP_2.46.F5.wireOp",EDGE,"E2.top"),sQuery(id+"FMMGtIccV8ZqxvP_2.46.F5.wireOp",EDGE,"E2.left"),sQuery(id+"FMMGtIccV8ZqxvP_2.47.F5.wireOp",EDGE,"E2.bottom"),sQuery(id+"FMMGtIccV8ZqxvP_2.47.F5.wireOp",EDGE,"E2.top"),sQuery(id+"FMMGtIccV8ZqxvP_2.47.F5.wireOp",EDGE,"E2.left"),sQuery(id+"FMMGtIccV8ZqxvP_2.48.F5.wireOp",EDGE,"E2.bottom"),sQuery(id+"FMMGtIccV8ZqxvP_2.48.F5.wireOp",EDGE,"E2.top"),sQuery(id+"FMMGtIccV8ZqxvP_2.48.F5.wireOp",EDGE,"E2.left"),sQuery(id+"FMMGtIccV8ZqxvP_2.49.F5.wireOp",EDGE,"E2.bottom"),sQuery(id+"FMMGtIccV8ZqxvP_2.49.F5.wireOp",EDGE,"E2.top"),sQuery(id+"FMMGtIccV8ZqxvP_2.49.F5.wireOp",EDGE,"E2.left"),sQuery(id+"F8.wireOp",EDGE,"E4")])],"isStart":false});
            var sketch = newSketch(context, id + "F10", { "sketchPlane" : qUnion([Q0])});
            skCircle(sketch, "E5", {"center": v(0, 0) * mm, "radius": 42.25 * mm});
            skSolve(sketch);
        }
        {
            var Q0;
            Q0=makeQuery(id+"F10.imprint","IMPRINT",FACE,{"disambiguationData":[TD([[makeQuery(id+"F10.imprint","IMPRINT",EDGE,{"derivedFrom":sQuery(id+"F10.wireOp",EDGE,"E5")}),1.0]])]});
            extrude(context, id + "F11", {"entities" : qUnion([Q0]), "depth" : 50.5 * mm});
        }
        {
            var Q0;
            Q0=makeQuery(id+"F11.opExtrude","CAP_FACE",FACE,{"disambiguationData":[OSD([sQuery(id+"F8.wireOp",EDGE,"E4"),sQuery(id+"F10.wireOp",EDGE,"E5")])],"isStart":false});
            var sketch = newSketch(context, id + "F12", { "sketchPlane" : qUnion([Q0])});
            skCircle(sketch, "E6", {"center": v(0, 0) * mm, "radius": 40.25 * mm});
            skSolve(sketch);
        }
        {
            var Q0;
            Q0=makeQuery(id+"F12.imprint","IMPRINT",FACE,{"disambiguationData":[TD([[makeQuery(id+"F12.imprint","IMPRINT",EDGE,{"derivedFrom":sQuery(id+"F12.wireOp",EDGE,"E6")}),1.0]])]});
            extrude(context, id + "F13", {"entities" : qUnion([Q0]), "operationType" : NewBodyOperationType.ADD, "depth" : 19 * mm});
        }
        {
            var Q0;
            Q0=makeQuery(id+"F13.opExtrude","CAP_FACE",FACE,{"disambiguationData":[OSD([sQuery(id+"F8.wireOp",EDGE,"E4"),sQuery(id+"F12.wireOp",EDGE,"E6")])],"isStart":false});
            var sketch = newSketch(context, id + "F14", { "sketchPlane" : qUnion([Q0])});
            skCircle(sketch, "E7", {"center": v(0, 0) * mm, "radius": 41.25 * mm});
            skSolve(sketch);
        }
        {
            var Q0;
            Q0=makeQuery(id+"F14.imprint","IMPRINT",FACE,{"disambiguationData":[TD([[makeQuery(id+"F14.imprint","IMPRINT",EDGE,{"derivedFrom":sQuery(id+"F14.wireOp",EDGE,"E7")}),1.0]])]});
            extrude(context, id + "F15", {"entities" : qUnion([Q0]), "depth" : 82.5 * mm});
        }
        {
            var Q0;
            Q0=makeQuery(id+"F15.opExtrude","CAP_FACE",FACE,{"disambiguationData":[OSD([sQuery(id+"F12.wireOp",EDGE,"E6"),sQuery(id+"F14.wireOp",EDGE,"E7")])],"isStart":false});
            var sketch = newSketch(context, id + "F16", { "sketchPlane" : qUnion([Q0])});
            skCircle(sketch, "E8", {"center": v(0, 0) * mm, "radius": 41.25 * mm});
            skSolve(sketch);
        }
        {
            var Q0;
            Q0=makeQuery(id+"F16.imprint","IMPRINT",FACE,{"disambiguationData":[TD([[makeQuery(id+"F16.imprint","IMPRINT",EDGE,{"derivedFrom":makeQuery(id+"F15.opExtrude","CAP_EDGE",EDGE,{"disambiguationData":[OSD([sQuery(id+"F12.wireOp",EDGE,"E6")])],"isStart":false})}),1.0]])]});
            extrude(context, id + "F17", {"entities" : qUnion([Q0]), "operationType" : NewBodyOperationType.ADD, "oppositeDirection" : true, "depth" : 2 * mm});
        }
        {
            var Q0;
            Q0=qCreatedBy(makeId("Right.planeOp"),FACE);
            var sketch = newSketch(context, id + "F18", { "sketchPlane" : qUnion([Q0])});
            skLineSegment(sketch, "E9.bottom", {"start": v(56.31, 78) * mm, "end": v(49.31, 78) * mm});
            skLineSegment(sketch, "E9.top", {"start": v(56.31, 74) * mm, "end": v(49.31, 74) * mm});
            skLineSegment(sketch, "E9.left", {"start": v(56.31, 78) * mm, "end": v(56.31, 74) * mm});
            skLineSegment(sketch, "E9.right", {"start": v(49.31, 78) * mm, "end": v(49.31, 74) * mm});
            skSolve(sketch);
        }
        {
            var Q0;
            Q0=makeQuery(id+"F18.imprint","IMPRINT",FACE,{"disambiguationData":[TD([[makeQuery(id+"F18.imprint","IMPRINT",EDGE,{"derivedFrom":sQuery(id+"F18.wireOp",EDGE,"E9.bottom")}),1.0]])]});
            extrude(context, id + "F19", {"entities" : qUnion([Q0]), "endBound" : BoundingType.SYMMETRIC, "depth" : 2 * mm});
        }
        {
            var Q0;
            Q0=makeQuery(id+"F19.opExtrude","SWEPT_BODY",BODY,{"disambiguationData":[OSD([sQuery(id+"F18.wireOp",EDGE,"E9.bottom"),sQuery(id+"F18.wireOp",EDGE,"E9.top"),sQuery(id+"F18.wireOp",EDGE,"E9.left"),sQuery(id+"F18.wireOp",EDGE,"E9.right")])]});
            transform(context, id + "F20", {"entities" : qUnion([Q0]), "transformType" : TransformType.TRANSLATION_3D, "dx" : 0 * mm, "dy" : -7.2 * mm, "dz" : 0 * mm, "makeCopy" : false});
        }
    });
